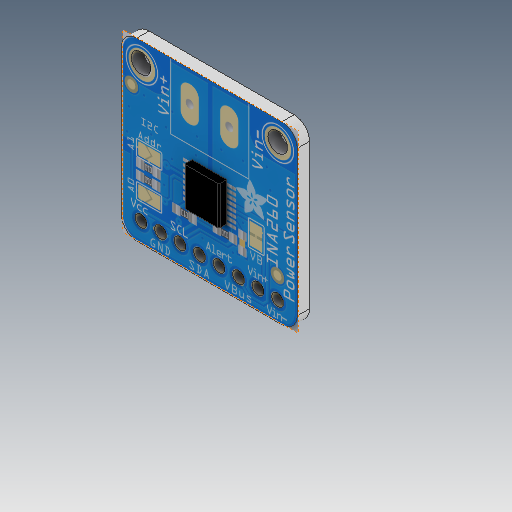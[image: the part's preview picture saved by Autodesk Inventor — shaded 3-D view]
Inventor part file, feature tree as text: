
AUTODESK INVENTOR PART (.ipt)
format: ipt  version: 2020 (Build 240168000, 168)  size: 389,632 bytes
history: native  units: in
note: dims shown in document units (in); Inventor stores cm internally (conversion verified against a paired STEP export)
features: sketch x3, extrude x2, fillet x1, chamfer x1, other x1
ambient origin geometry x8: Origin, YZ Plane, XZ Plane, XY Plane, X Axis, Y Axis, Z Axis, Center Point
bodies: Solid1 (feature_tree)
feature tree (8):
  extrude  "Extrusion1"  Depth=0.9in
  fillet  "Fillet1"  Radius=0.1in
  extrude  "Extrusion2"  Depth=0.8in
  chamfer  "Chamfer1"  Distance=0.1in
  sketch  "Sketch5"  dims[d5=0.06in d6=0.1in d7=3.1496in d9=0.1in d10=0.3937in d12=1.0in d14=0.063in d15=0.0in d16=0.0787in d17=0.1772in d18=0.1969in d20=0.502in d21=0.0394in d22=0.0in d23=0.0079in d24=0.0787in d25=45.0deg]
  sketch  "Sketch1"  dims[d0=0.9in d1=0.9in d2=0.1in]
  sketch  "Sketch2"  dims[d3=0.7in d4=0.8in]
  other  "Image4"
